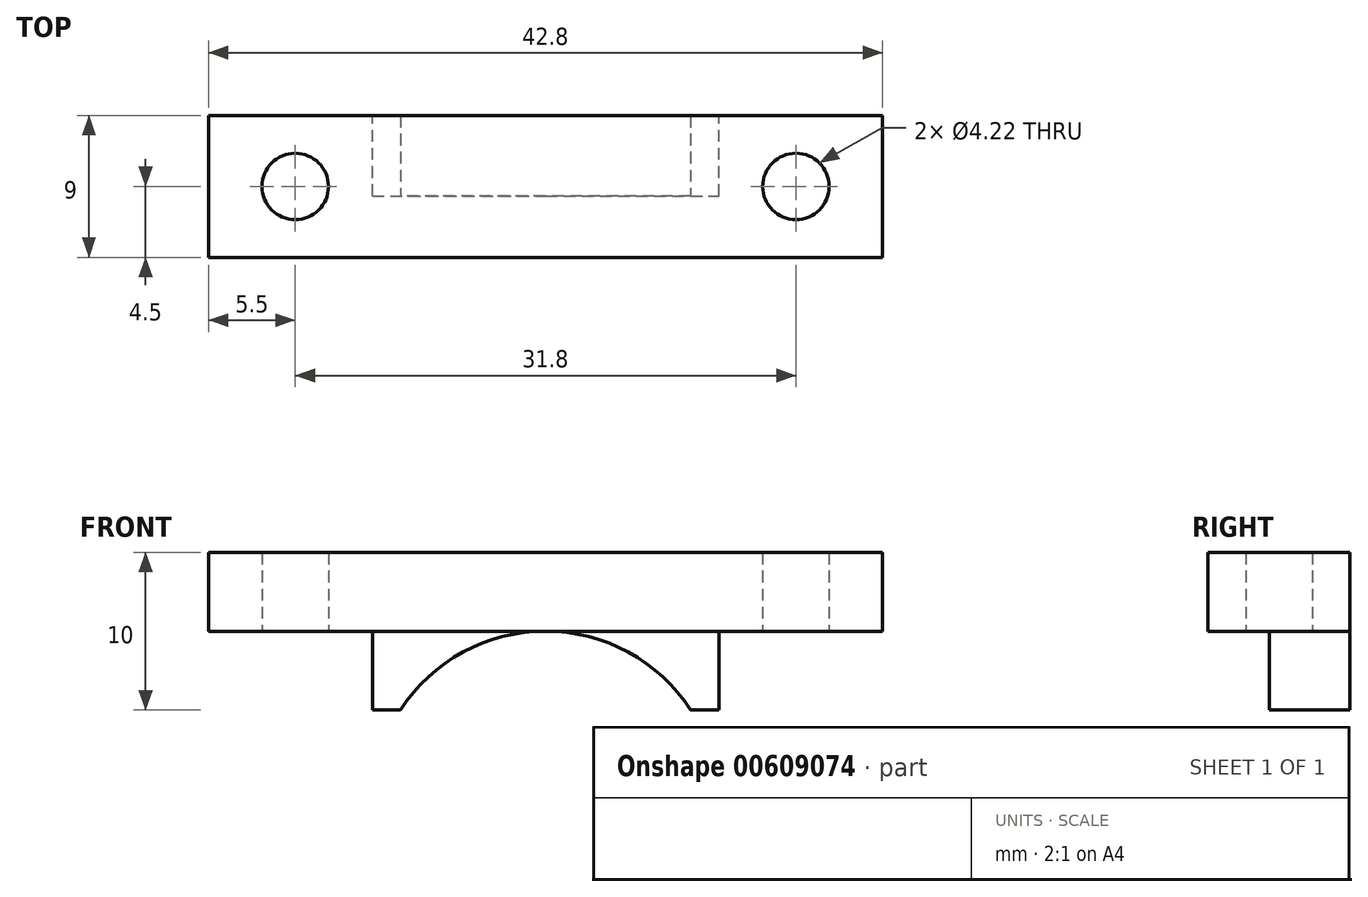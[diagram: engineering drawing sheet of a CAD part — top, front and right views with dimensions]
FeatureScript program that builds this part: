
annotation { "Feature Type Name" : "Feature", "Feature Type Description" : "" }
export const myFeature = defineFeature(function(context is Context, id is Id, definition is map)
    precondition{}
    {
        {
            var Q0;
            Q0=qCreatedBy(makeId("Top.planeOp"),FACE);
            var sketch = newSketch(context, id + "F0", { "sketchPlane" : qUnion([Q0])});
            skLineSegment(sketch, "E0.bottom", {"start": v(-21.4, 4.5) * mm, "end": v(21.4, 4.5) * mm});
            skLineSegment(sketch, "E0.top", {"start": v(-21.4, -4.5) * mm, "end": v(21.4, -4.5) * mm});
            skLineSegment(sketch, "E0.left", {"start": v(-21.4, 4.5) * mm, "end": v(-21.4, -4.5) * mm});
            skLineSegment(sketch, "E0.right", {"start": v(21.4, 4.5) * mm, "end": v(21.4, -4.5) * mm});
            skPoint(sketch, "E0.middle", {"position": v(0, 0) * mm});
            skSolve(sketch);
        }
        {
            var Q0;
            Q0=makeQuery(id+"F0.imprint","IMPRINT",FACE,{"disambiguationData":[TD([[makeQuery(id+"F0.imprint","IMPRINT",EDGE,{"derivedFrom":sQuery(id+"F0.wireOp",EDGE,"E0.bottom")}),-1.0]])]});
            var sketch = newSketch(context, id + "F1", { "sketchPlane" : qUnion([Q0])});
            skCircle(sketch, "E1", {"center": v(-15.9, 0) * mm, "radius": 2.1 * mm});
            skCircle(sketch, "E2", {"center": v(15.9, 0) * mm, "radius": 2.1 * mm});
            skSolve(sketch);
        }
        {
            var Q0;
            Q0=makeQuery(id+"F0.imprint","IMPRINT",FACE,{"disambiguationData":[TD([[makeQuery(id+"F0.imprint","IMPRINT",EDGE,{"derivedFrom":sQuery(id+"F0.wireOp",EDGE,"E0.bottom")}),-1.0]])]});
            var sketch = newSketch(context, id + "F2", { "sketchPlane" : qUnion([Q0])});
            skLineSegment(sketch, "E3.bottom", {"start": v(-11, -0.6) * mm, "end": v(11, -0.6) * mm});
            skLineSegment(sketch, "E3.top", {"start": v(-11, 9.4) * mm, "end": v(11, 9.4) * mm});
            skLineSegment(sketch, "E3.left", {"start": v(-11, -0.6) * mm, "end": v(-11, 9.4) * mm});
            skLineSegment(sketch, "E3.right", {"start": v(11, -0.6) * mm, "end": v(11, 9.4) * mm});
            skPoint(sketch, "E3.middle", {"position": v(0, 4.4) * mm});
            skSolve(sketch);
        }
        {
            var Q0;
            Q0=makeQuery(id+"F0.imprint","IMPRINT",FACE,{"disambiguationData":[TD([[makeQuery(id+"F0.imprint","IMPRINT",EDGE,{"derivedFrom":sQuery(id+"F0.wireOp",EDGE,"E0.bottom")}),-1.0]])]});
            extrude(context, id + "F3", {"entities" : qUnion([Q0]), "depth" : 5 * mm, "offsetDistance" : 25 * mm});
        }
        {
            var Q0;
            Q0=makeQuery(id+"F1.imprint","IMPRINT",FACE,{"disambiguationData":[TD([[makeQuery(id+"F1.imprint","IMPRINT",EDGE,{"derivedFrom":sQuery(id+"F1.wireOp",EDGE,"E1")}),1.0]])]});
            var Q1;
            Q1=makeQuery(id+"F1.imprint","IMPRINT",FACE,{"disambiguationData":[TD([[makeQuery(id+"F1.imprint","IMPRINT",EDGE,{"derivedFrom":sQuery(id+"F1.wireOp",EDGE,"E2")}),1.0]])]});
            extrude(context, id + "F4", {"entities" : qUnion([Q0, Q1]), "operationType" : NewBodyOperationType.REMOVE, "depth" : 7 * mm, "offsetDistance" : 25 * mm});
        }
        {
            var Q0;
            {var subQ0=sQuery(id+"F2.wireOp",EDGE,"E3.bottom");Q0=makeQuery(id+"F2.imprint","IMPRINT",FACE,{"disambiguationData":[TD([[makeQuery(id+"F2.imprint","IMPRINT",EDGE,{"derivedFrom":subQ0}),1.0]])]});}
            extrude(context, id + "F5", {"entities" : qUnion([Q0]), "operationType" : NewBodyOperationType.ADD, "oppositeDirection" : true, "depth" : 5 * mm, "offsetDistance" : 25 * mm});
        }
        {
            var Q0;
            Q0=makeQuery(id+"F5.opExtrude","SWEPT_FACE",FACE,{"disambiguationData":[OSD([sQuery(id+"F2.wireOp",EDGE,"E3.bottom")])]});
            var sketch = newSketch(context, id + "F6", { "sketchPlane" : qUnion([Q0])});
            skCircle(sketch, "E4", {"center": v(0, -11) * mm, "radius": 11 * mm});
            skSolve(sketch);
        }
        {
            var Q0;
            {var subQ0=sQuery(id+"F6.wireOp",EDGE,"E4");var subQ1=sQuery(id+"F2.wireOp",EDGE,"E3.bottom");var subQ2=makeQuery(id+"F6.imprint","INTERSECT",VERTEX,{"derivedFrom":[makeQuery(id+"F5.opExtrude","CAP_EDGE",EDGE,{"disambiguationData":[OSD([subQ1])],"isStart":true}),subQ0]});Q0=makeQuery(id+"F6.imprint","IMPRINT",FACE,{"disambiguationData":[TD([[makeQuery(id+"F6.imprint","IMPRINT",EDGE,{"disambiguationData":[TD([[subQ2,1.0]])],"derivedFrom":subQ0}),1.0]])]});}
            extrude(context, id + "F7", {"entities" : qUnion([Q0]), "operationType" : NewBodyOperationType.REMOVE, "oppositeDirection" : true, "depth" : 7.1 * mm, "offsetDistance" : 25 * mm});
        }
    });
